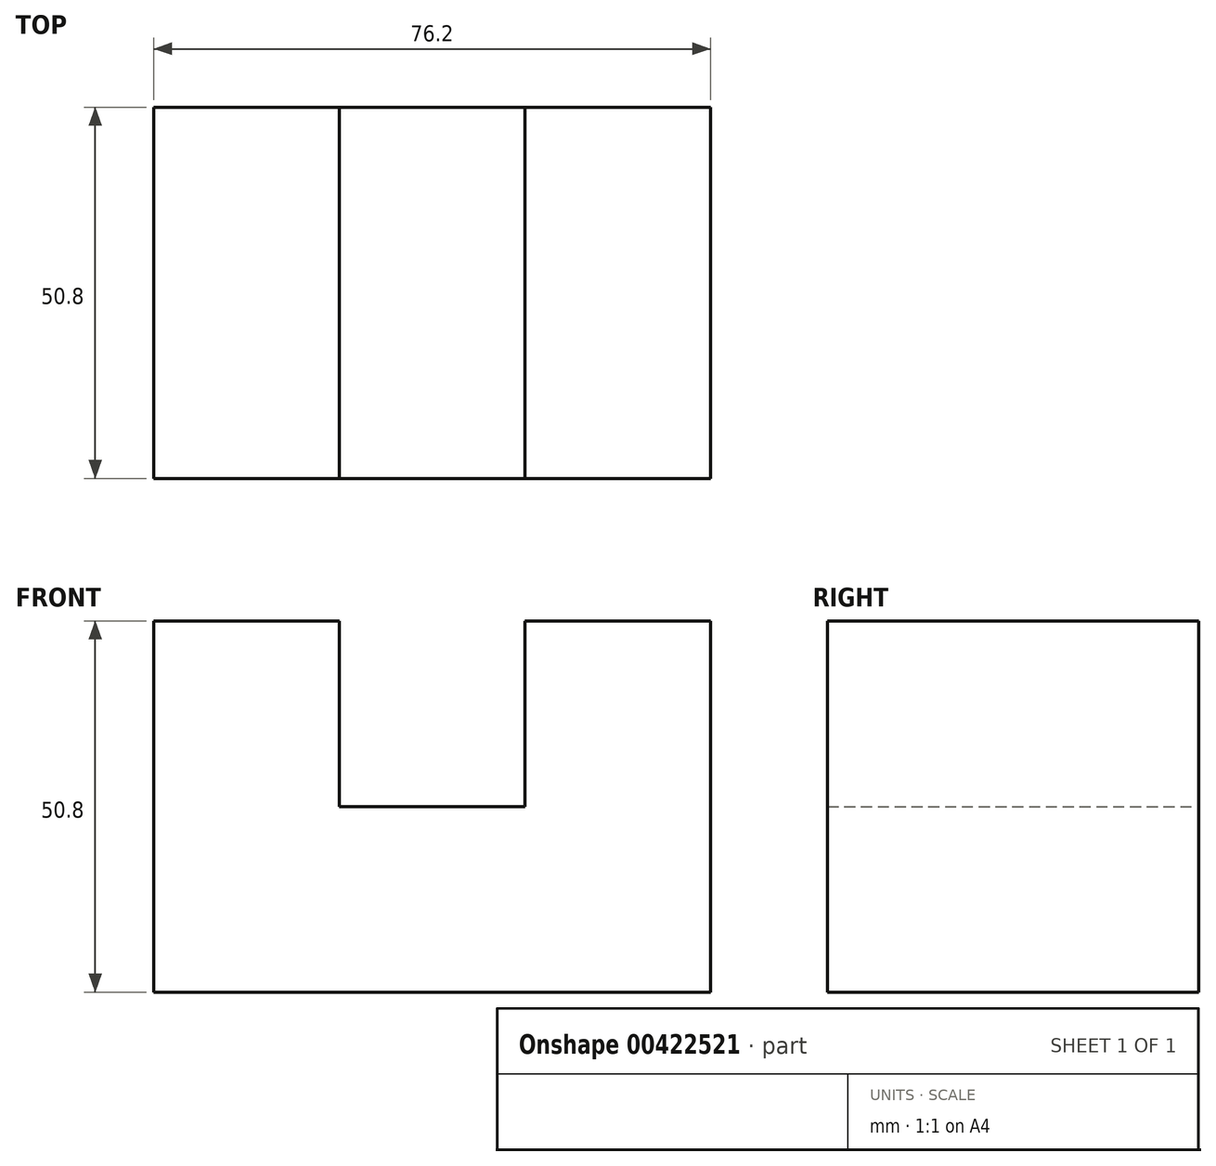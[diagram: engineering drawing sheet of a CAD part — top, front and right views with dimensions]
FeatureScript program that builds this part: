
annotation { "Feature Type Name" : "Feature", "Feature Type Description" : "" }
export const myFeature = defineFeature(function(context is Context, id is Id, definition is map)
    precondition{}
    {
        {
            var Q0;
            Q0=qCreatedBy(makeId("Front.planeOp"),FACE);
            var sketch = newSketch(context, id + "F0", { "sketchPlane" : qUnion([Q0])});
            skLineSegment(sketch, "E0", {"start": v(0, 0) * mm, "end": v(0, 50.8) * mm});
            skLineSegment(sketch, "E1", {"start": v(0, 50.8) * mm, "end": v(-25.4, 50.8) * mm});
            skLineSegment(sketch, "E2", {"start": v(-25.4, 50.8) * mm, "end": v(-25.4, 25.4) * mm});
            skLineSegment(sketch, "E3", {"start": v(-25.4, 25.4) * mm, "end": v(-50.8, 25.4) * mm});
            skLineSegment(sketch, "E4", {"start": v(-50.8, 25.4) * mm, "end": v(-50.8, 50.8) * mm});
            skLineSegment(sketch, "E5", {"start": v(-50.8, 50.8) * mm, "end": v(-76.2, 50.8) * mm});
            skLineSegment(sketch, "E6", {"start": v(-76.2, 50.8) * mm, "end": v(-76.2, 0) * mm});
            skLineSegment(sketch, "E7", {"start": v(-76.2, 0) * mm, "end": v(0, 0) * mm});
            skSolve(sketch);
        }
        {
            var Q0;
            Q0 = qSketchRegion(id + "F0", true);
            extrude(context, id + "F1", {"entities" : qUnion([Q0]), "depth" : 50.8 * mm});
        }
    });
